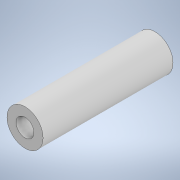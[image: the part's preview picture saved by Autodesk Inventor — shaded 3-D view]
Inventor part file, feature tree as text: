
AUTODESK INVENTOR PART (.ipt)
format: ipt  version: 2020 (Build 240168000, 168)  size: 95,232 bytes
history: native  units: in
note: dims shown in document units (in); Inventor stores cm internally (conversion verified against a paired STEP export)
features: extrude x1, sketch x1
ambient origin geometry x8: Origin, YZ Plane, XZ Plane, XY Plane, X Axis, Y Axis, Z Axis, Center Point
bodies: Solid1 (feature_tree)
feature tree (2):
  extrude  "Extrusion1"  Depth=0.3937in
  sketch  "Sketch1"  dims[d0=0.1949in d3=0.3937in d4=1.4173in d5=0.0in]
